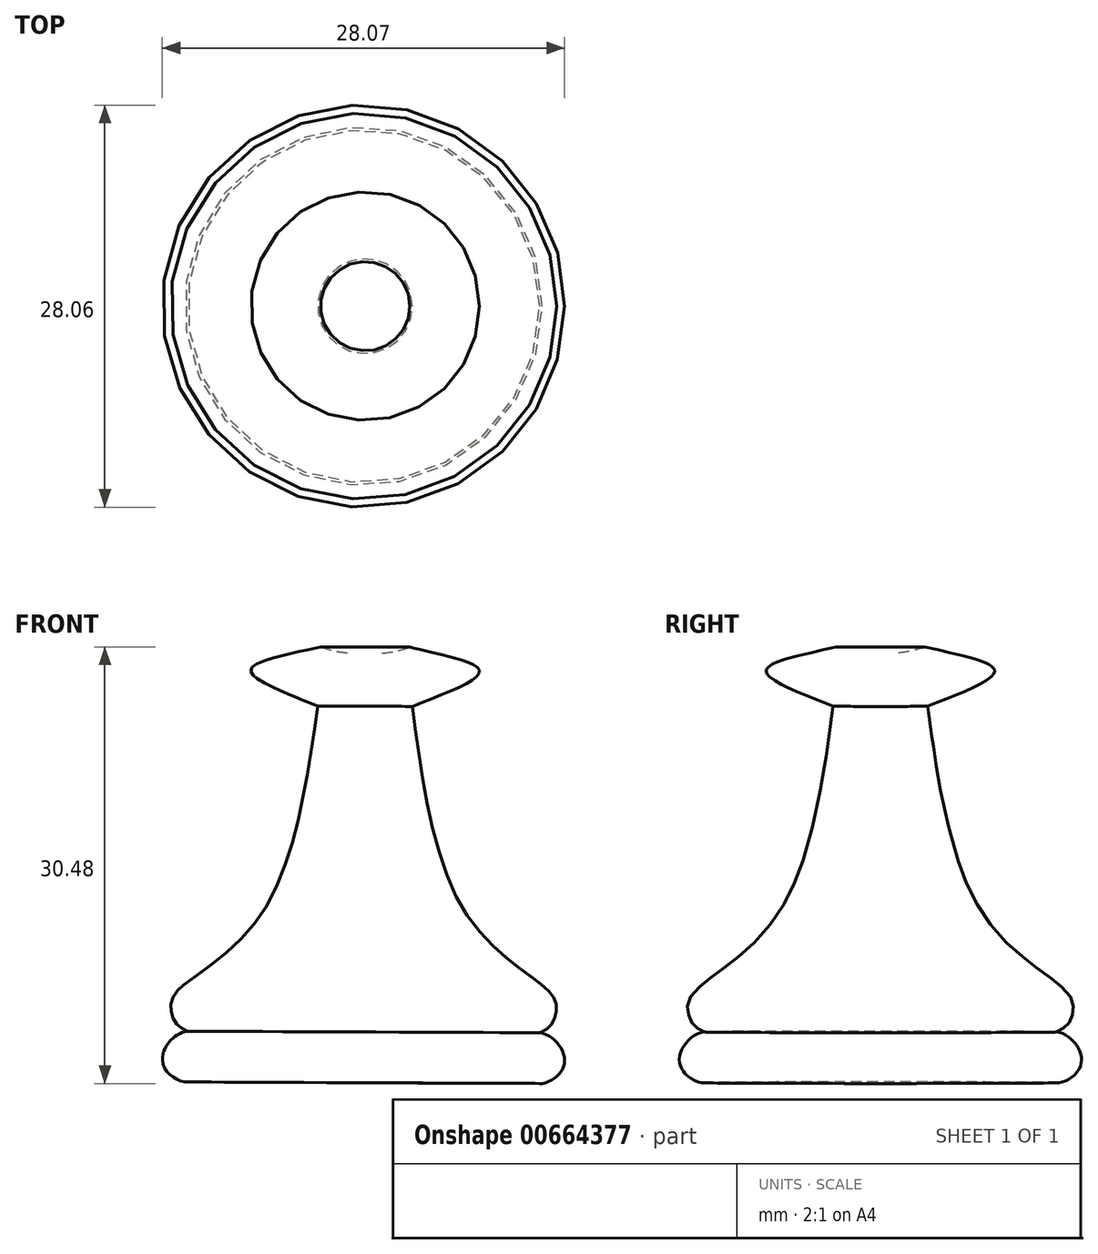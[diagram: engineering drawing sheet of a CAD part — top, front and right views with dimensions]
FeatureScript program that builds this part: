
annotation { "Feature Type Name" : "Feature", "Feature Type Description" : "" }
export const myFeature = defineFeature(function(context is Context, id is Id, definition is map)
    precondition{}
    {
        {
            var Q0;
            Q0=qCreatedBy(makeId("Front.planeOp"),FACE);
            var sketch = newSketch(context, id + "F0", { "sketchPlane" : qUnion([Q0])});
            skLineSegment(sketch, "E0", {"start": v(1.06, 2) * mm, "end": v(13.54, 1.96) * mm});
            skArc(sketch, "E1", {"start": v(4.3, 32.41) * mm, "mid": v(9.09, 40.96) * mm, "end": v(1.25, 46.84) * mm});
            skFitSpline(sketch, "E2", {"points": [v(4.3, 32.41) * mm, v(6.97, 31.78) * mm, v(9.16, 30.71) * mm, v(4.47, 28.28) * mm], "startDerivative": vector(7.34, -1.75) * mm, "endDerivative": vector(-15.08, -5.99) * mm});
            skPoint(sketch, "E3", {"position": v(13.54, 1.96) * mm});
            skFitSpline(sketch, "E4", {"points": [v(13.54, 1.96) * mm, v(15.1, 3.58) * mm, v(13.36, 5.5) * mm], "startDerivative": vector(5.3, 1.1) * mm, "endDerivative": vector(-5.13, 0.56) * mm});
            skFitSpline(sketch, "E5", {"points": [v(13.36, 5.5) * mm, v(14.3, 6.27) * mm, v(14.5, 7.54) * mm, v(13.36, 8.97) * mm, v(8.05, 14.09) * mm, v(4.47, 28.28) * mm], "startDerivative": vector(13.23, 5.62) * mm, "endDerivative": vector(-4.65, 34.76) * mm});
            skLineSegment(sketch, "E6", {"start": v(1.25, 46.84) * mm, "end": v(1.06, 2) * mm});
            skSolve(sketch);
        }
        {
            var Q0;
            Q0=makeQuery(id+"F0.imprint","IMPRINT",FACE,{"disambiguationData":[TD([[makeQuery(id+"F0.imprint","IMPRINT",EDGE,{"derivedFrom":sQuery(id+"F0.wireOp",EDGE,"E0")}),1.0]])]});
            var Q1;
            Q1=sQuery(id+"F0.wireOp",EDGE,"E6");
            revolve(context, id + "F1", {"surfaceOperationType" : NewSurfaceOperationType.NEW, "entities" : qUnion([Q0]), "axis" : qUnion([Q1]), "revolveType" : RevolveType.FULL});
        }
    });
